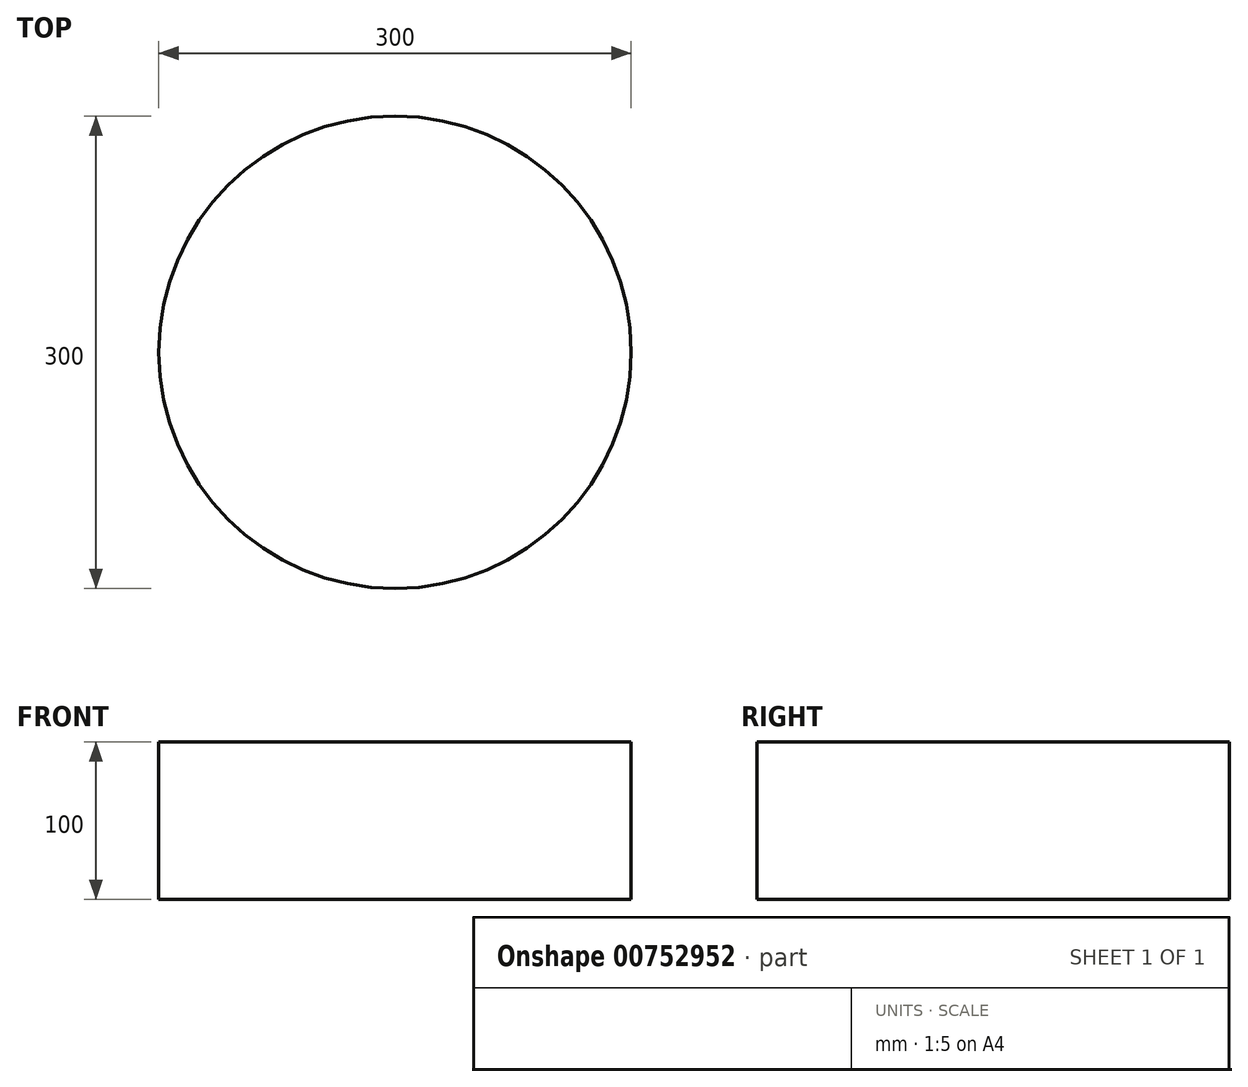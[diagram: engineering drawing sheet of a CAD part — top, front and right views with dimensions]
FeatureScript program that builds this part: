
annotation { "Feature Type Name" : "Feature", "Feature Type Description" : "" }
export const myFeature = defineFeature(function(context is Context, id is Id, definition is map)
    precondition{}
    {
        {
            var Q0;
            Q0=qCreatedBy(makeId("Top.planeOp"),FACE);
            var sketch = newSketch(context, id + "F0", { "sketchPlane" : qUnion([Q0])});
            skCircle(sketch, "E0", {"center": v(0, 0) * mm, "radius": 150 * mm});
            skSolve(sketch);
        }
        {
            var Q0;
            Q0=makeQuery(id+"F0.imprint","IMPRINT",FACE,{"disambiguationData":[TD([[makeQuery(id+"F0.imprint","IMPRINT",EDGE,{"derivedFrom":sQuery(id+"F0.wireOp",EDGE,"E0")}),1.0]])]});
            extrude(context, id + "F1", {"entities" : qUnion([Q0]), "depth" : 100 * mm, "offsetDistance" : 25 * mm});
        }
    });
